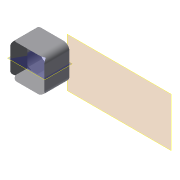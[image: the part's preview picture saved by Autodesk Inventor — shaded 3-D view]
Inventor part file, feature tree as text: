
AUTODESK INVENTOR PART (.ipt)
format: ipt  version: 2019.4 (Build 234330000, 330)  size: 209,408 bytes
history: native  units: mm
features: extrude x4, sketch x4, other x4, reference x3, plane x2, projected_geometry x2, pattern_circular x1, fillet x1
ambient origin geometry x8: Origin, YZ Plane, XZ Plane, XY Plane, X Axis, Y Axis, Z Axis, Center Point
bodies: Solid1 (feature_tree)
feature tree (21):
  plane  "Work Plane1"
  extrude  "Extrusion1"  Depth=27.0mm
  extrude  "Extrusion2"  Depth=29.0mm
  extrude  "Extrusion4"  Depth=10.0mm TaperAngle=0.0deg
  pattern_circular  "Circular Pattern1"  Count=4 Angle=360.0deg
  fillet  "Fillet1"  Radius=5.0mm
  plane  "Work Plane2"
  extrude  "Extrusion5"  Depth=5.0mm
  sketch  "Sketch1"  dims[d0=0.5mm d1=27.0mm]
  reference  "Reference1"
  reference  "Reference2"
  sketch  "Sketch2"  dims[d2=12.0mm d3=0.0mm d4=29.0mm]
  projected_geometry  "Projected Loop1"
  sketch  "Sketch4"  dims[d5=29.0mm d6=10.0mm d7=0.0mm]
  reference  "Reference5"
  projected_geometry  "Projected Loop4"
  sketch  "Sketch5"  dims[d13=1.0mm d14=0.0mm d15=40.0mm d16=360.0deg d18=5.0mm d19=6.0mm d20=6.0mm d21=2.8mm d22=2.8mm d23=0.0mm]
  other  "Assembly_Opentrons_Autofocus_v2.iam"
  other  "00_objectivelens_10x:1"
  other  "01_Slide_camera_v1:1"
  other  "00_LED_neopixel_single:1"
